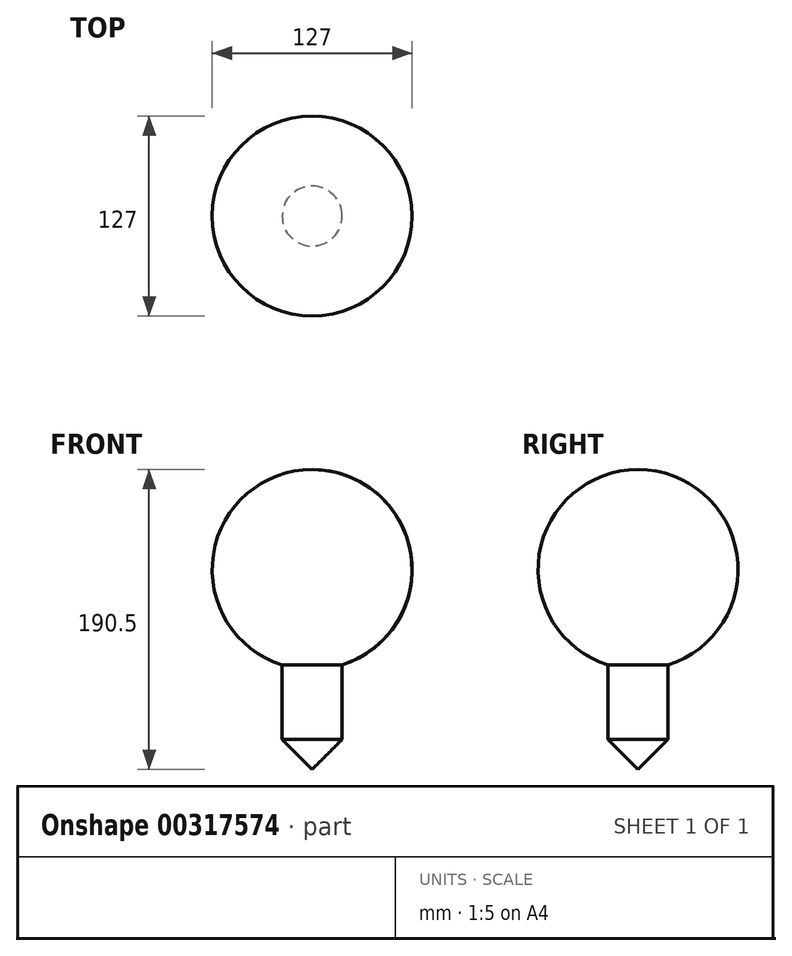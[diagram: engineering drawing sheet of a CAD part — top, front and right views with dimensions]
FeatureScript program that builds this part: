
annotation { "Feature Type Name" : "Feature", "Feature Type Description" : "" }
export const myFeature = defineFeature(function(context is Context, id is Id, definition is map)
    precondition{}
    {
        {
            var Q0;
            Q0=qCreatedBy(makeId("Front.planeOp"),FACE);
            var sketch = newSketch(context, id + "F0", { "sketchPlane" : qUnion([Q0])});
            skArc(sketch, "E0", {"start": v(0, 63.5) * mm, "mid": v(-63.5, 0) * mm, "end": v(0, -63.5) * mm});
            skLineSegment(sketch, "E1", {"start": v(0, 63.5) * mm, "end": v(0, -63.5) * mm});
            skPoint(sketch, "E2.orphan", {"position": v(0, 69.95) * mm});
            skSolve(sketch);
        }
        {
            var Q0;
            Q0=makeQuery(id+"F0.imprint","IMPRINT",FACE,{"disambiguationData":[TD([[makeQuery(id+"F0.imprint","IMPRINT",EDGE,{"derivedFrom":sQuery(id+"F0.wireOp",EDGE,"E0")}),1.0]])]});
            var Q1;
            Q1=sQuery(id+"F0.wireOp",EDGE,"E1");
            revolve(context, id + "F1", {"entities" : qUnion([Q0]), "axis" : qUnion([Q1]), "revolveType" : RevolveType.FULL});
        }
        {
            var Q0;
            Q0=qCreatedBy(makeId("Top.planeOp"),FACE);
            var sketch = newSketch(context, id + "F2", { "sketchPlane" : qUnion([Q0])});
            skCircle(sketch, "E3", {"center": v(0, 0) * mm, "radius": 19.05 * mm});
            skSolve(sketch);
        }
        {
            var Q0;
            Q0 = qSketchRegion(id + "F2", true);
            extrude(context, id + "F3", {"entities" : qUnion([Q0]), "operationType" : NewBodyOperationType.ADD, "oppositeDirection" : true, "depth" : 127 * mm});
        }
        {
            var Q0;
            Q0=makeQuery(id+"F3.opExtrude","CAP_EDGE",EDGE,{"disambiguationData":[OSD([sQuery(id+"F2.wireOp",EDGE,"E3")])],"isStart":false});
            chamfer(context, id + "F4", {"entities" : qUnion([Q0]), "width" : 19.05 * mm, "tangentPropagation" : true});
        }
    });
